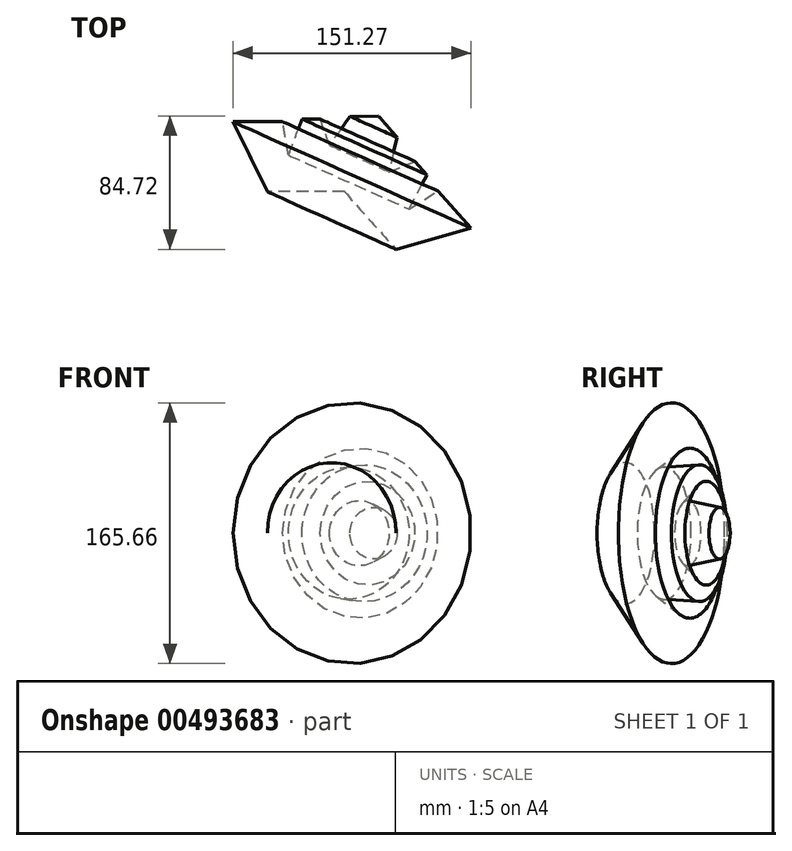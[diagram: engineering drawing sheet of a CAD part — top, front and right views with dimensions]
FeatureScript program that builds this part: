
annotation { "Feature Type Name" : "Feature", "Feature Type Description" : "" }
export const myFeature = defineFeature(function(context is Context, id is Id, definition is map)
    precondition{}
    {
        {
            var Q0;
            Q0=qCreatedBy(makeId("Top.planeOp"),FACE);
            var sketch = newSketch(context, id + "F0", { "sketchPlane" : qUnion([Q0])});
            skLineSegment(sketch, "E0", {"start": v(-43.9, 34.57) * mm, "end": v(-12.34, 34.57) * mm});
            skLineSegment(sketch, "E1", {"start": v(-12.34, 34.57) * mm, "end": v(-8.6, 13.34) * mm});
            skLineSegment(sketch, "E2", {"start": v(-8.6, 13.34) * mm, "end": v(0, 36.3) * mm});
            skLineSegment(sketch, "E3", {"start": v(0, 36.3) * mm, "end": v(11.48, 36.3) * mm});
            skLineSegment(sketch, "E4", {"start": v(11.48, 36.3) * mm, "end": v(17.5, 19.65) * mm});
            skLineSegment(sketch, "E5", {"start": v(17.5, 19.65) * mm, "end": v(30.4, 38.01) * mm});
            skLineSegment(sketch, "E6", {"start": v(30.4, 38.01) * mm, "end": v(48.48, 38.3) * mm});
            skLineSegment(sketch, "E7", {"start": v(48.48, 38.3) * mm, "end": v(26.97, -9.9) * mm});
            skLineSegment(sketch, "E8", {"start": v(26.97, -9.9) * mm, "end": v(-22.1, -9.9) * mm});
            skLineSegment(sketch, "E9", {"start": v(-22.1, -9.9) * mm, "end": v(-43.9, 34.57) * mm});
            skSolve(sketch);
        }
        {
            var Q0;
            Q0=makeQuery(id+"F0.imprint","IMPRINT",FACE,{"disambiguationData":[TD([[makeQuery(id+"F0.imprint","IMPRINT",EDGE,{"derivedFrom":sQuery(id+"F0.wireOp",EDGE,"E0")}),-1.0]])]});
            var Q1;
            Q1=sQuery(id+"F0.wireOp",EDGE,"E7");
            revolve(context, id + "F1", {"entities" : qUnion([Q0]), "axis" : qUnion([Q1]), "revolveType" : RevolveType.FULL});
        }
    });
